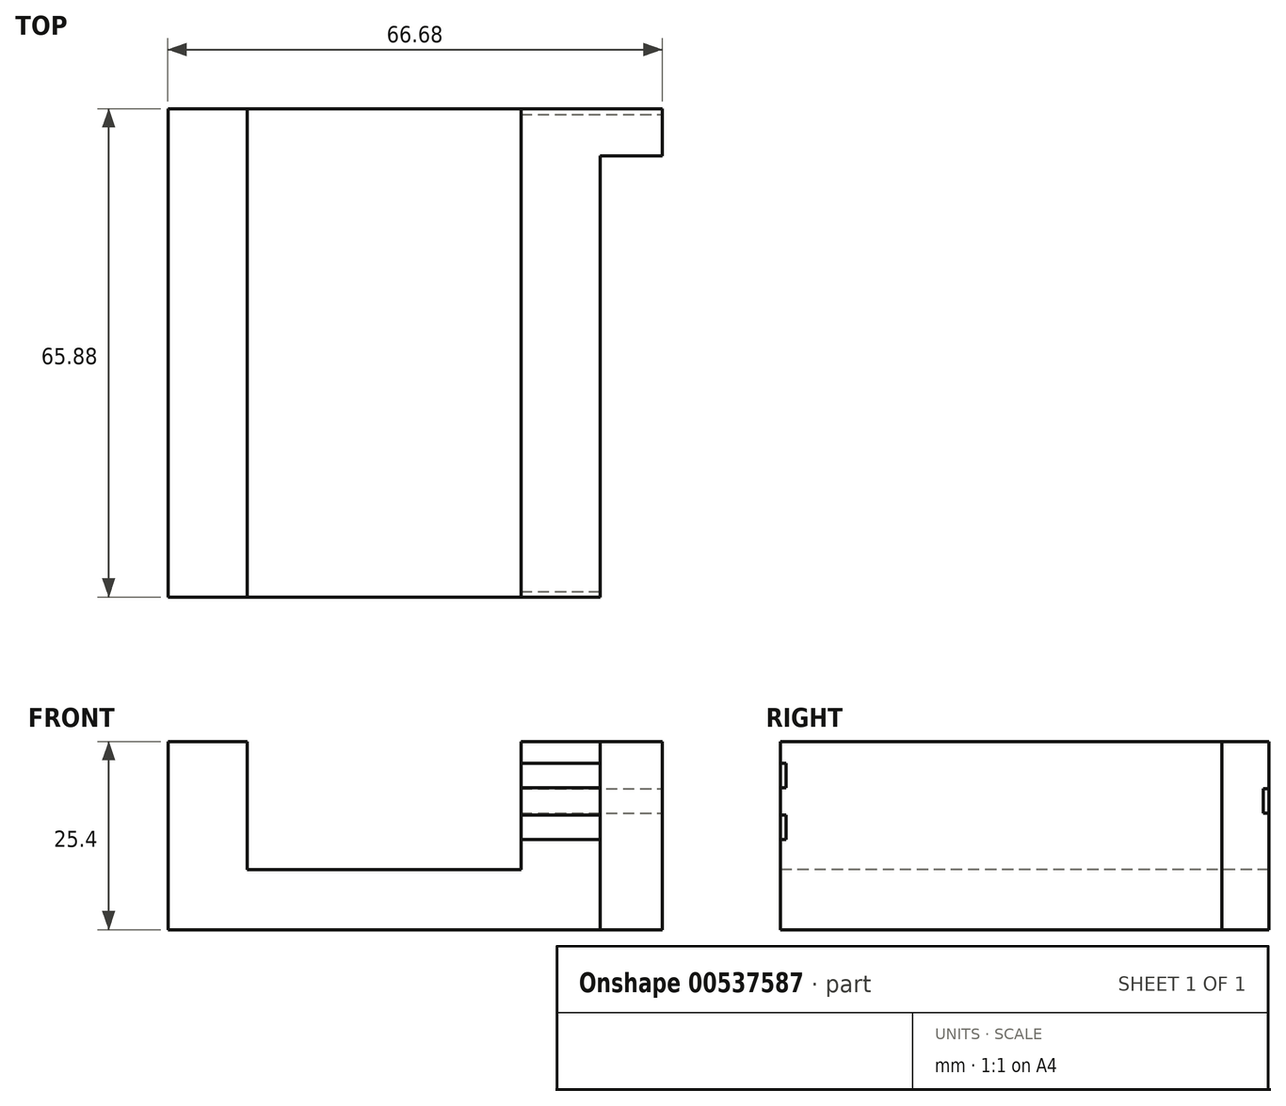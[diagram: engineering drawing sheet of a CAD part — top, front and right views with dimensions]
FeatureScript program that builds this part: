
annotation { "Feature Type Name" : "Feature", "Feature Type Description" : "" }
export const myFeature = defineFeature(function(context is Context, id is Id, definition is map)
    precondition{}
    {
        {
            var Q0;
            Q0=qCreatedBy(makeId("Top.planeOp"),FACE);
            var sketch = newSketch(context, id + "F0", { "sketchPlane" : qUnion([Q0])});
            skLineSegment(sketch, "E0.bottom", {"start": v(29.15, 32.94) * mm, "end": v(-1.9, 32.94) * mm});
            skLineSegment(sketch, "E0.top", {"start": v(29.15, -32.94) * mm, "end": v(9.65, -32.94) * mm});
            skLineSegment(sketch, "E0.right", {"start": v(-29.15, 32.94) * mm, "end": v(-29.15, -32.94) * mm});
            skPoint(sketch, "E0.middle", {"position": v(0, 0) * mm});
            skLineSegment(sketch, "E1", {"start": v(-18.48, 32.94) * mm, "end": v(-18.48, -32.94) * mm});
            skLineSegment(sketch, "E2", {"start": v(18.48, 32.94) * mm, "end": v(18.48, -32.94) * mm});
            skLineSegment(sketch, "E3.trimOffspring", {"start": v(-1.9, 32.94) * mm, "end": v(-29.15, 32.94) * mm});
            skLineSegment(sketch, "E4.trimOffspring", {"start": v(9.65, -32.94) * mm, "end": v(-9.65, -32.94) * mm});
            skLineSegment(sketch, "E5.trimOffspring", {"start": v(-9.65, -32.94) * mm, "end": v(-29.15, -32.94) * mm});
            skLineSegment(sketch, "E6", {"start": v(29.15, 32.94) * mm, "end": v(37.53, 32.94) * mm});
            skLineSegment(sketch, "E7", {"start": v(37.53, 32.94) * mm, "end": v(37.53, 26.6) * mm});
            skLineSegment(sketch, "E8", {"start": v(37.53, 26.6) * mm, "end": v(29.15, 26.6) * mm});
            skLineSegment(sketch, "E9", {"start": v(29.15, -20.24) * mm, "end": v(29.15, -32.94) * mm});
            skLineSegment(sketch, "E10", {"start": v(29.15, -20.24) * mm, "end": v(29.15, 32.94) * mm});
            skSolve(sketch);
        }
        {
            var Q0;
            {var subQ1=sQuery(id+"F0.wireOp",EDGE,"E1");Q0=makeQuery(id+"F0.imprint","IMPRINT",FACE,{"disambiguationData":[TD([[makeQuery(id+"F0.imprint","IMPRINT",EDGE,{"derivedFrom":subQ1}),1.0]])]});}
            extrude(context, id + "F1", {"entities" : qUnion([Q0]), "depth" : 8.13 * mm, "offsetDistance" : 25.4 * mm});
        }
        {
            var Q0;
            {var subQ0=sQuery(id+"F0.wireOp",EDGE,"E0.right");Q0=makeQuery(id+"F0.imprint","IMPRINT",FACE,{"disambiguationData":[TD([[makeQuery(id+"F0.imprint","IMPRINT",EDGE,{"derivedFrom":subQ0}),1.0]])]});}
            var Q1;
            {var subQ0=sQuery(id+"F0.wireOp",EDGE,"E0.left");Q1=makeQuery(id+"F0.imprint","IMPRINT",FACE,{"disambiguationData":[TD([[makeQuery(id+"F0.imprint","IMPRINT",EDGE,{"derivedFrom":subQ0}),-1.0]])]});}
            var Q2;
            {var subQ0=sQuery(id+"F0.wireOp",EDGE,"E6");Q2=makeQuery(id+"F0.imprint","IMPRINT",FACE,{"disambiguationData":[TD([[makeQuery(id+"F0.imprint","IMPRINT",EDGE,{"derivedFrom":subQ0}),-1.0]])]});}
            var Q3;
            {var subQ0=sQuery(id+"F0.wireOp",EDGE,"E2");Q3=makeQuery(id+"F0.imprint","IMPRINT",FACE,{"disambiguationData":[TD([[makeQuery(id+"F0.imprint","IMPRINT",EDGE,{"derivedFrom":subQ0}),1.0]])]});}
            extrude(context, id + "F2", {"entities" : qUnion([Q0, Q1, Q2, Q3]), "operationType" : NewBodyOperationType.ADD, "depth" : 25.4 * mm, "offsetDistance" : 25.4 * mm});
        }
        {
            var Q0;
            {var subQ0=sQuery(id+"F0.wireOp",EDGE,"E5.trimOffspring");var subQ1=sQuery(id+"F0.wireOp",EDGE,"E0.top");Q0=makeQuery(id+"F2.boolean.opBoolean","MERGE",FACE,{"derivedFrom":[makeQuery(id+"F1.opExtrude","SWEPT_FACE",FACE,{"disambiguationData":[OSD([subQ1,sQuery(id+"F0.wireOp",EDGE,"E4.trimOffspring"),subQ0])]}),makeQuery(id+"F2.opExtrude","SWEPT_FACE",FACE,{"disambiguationData":[OSD([subQ1])]}),makeQuery(id+"F2.opExtrude","SWEPT_FACE",FACE,{"disambiguationData":[OSD([subQ0])]})]});}
            var sketch = newSketch(context, id + "F3", { "sketchPlane" : qUnion([Q0])});
            skLineSegment(sketch, "E11", {"start": v(18.48, 22.48) * mm, "end": v(29.15, 22.48) * mm});
            skLineSegment(sketch, "E12", {"start": v(29.15, 19.18) * mm, "end": v(18.48, 19.18) * mm});
            skLineSegment(sketch, "E13", {"start": v(29.15, 15.5) * mm, "end": v(18.48, 15.5) * mm});
            skLineSegment(sketch, "E14", {"start": v(29.15, 12.2) * mm, "end": v(18.48, 12.2) * mm});
            skSolve(sketch);
        }
        {
            var Q0;
            {var subQ0=sQuery(id+"F3.wireOp",EDGE,"E13");Q0=makeQuery(id+"F3.imprint","IMPRINT",FACE,{"disambiguationData":[TD([[makeQuery(id+"F3.imprint","IMPRINT",EDGE,{"derivedFrom":subQ0}),1.0]])]});}
            var Q1;
            {var subQ0=sQuery(id+"F3.wireOp",EDGE,"E11");Q1=makeQuery(id+"F3.imprint","IMPRINT",FACE,{"disambiguationData":[TD([[makeQuery(id+"F3.imprint","IMPRINT",EDGE,{"derivedFrom":subQ0}),-1.0]])]});}
            extrude(context, id + "F4", {"entities" : qUnion([Q0, Q1]), "operationType" : NewBodyOperationType.REMOVE, "oppositeDirection" : true, "depth" : 0.76 * mm, "offsetDistance" : 25.4 * mm});
        }
        {
            var Q0;
            {var subQ0=sQuery(id+"F0.wireOp",EDGE,"E3.trimOffspring");var subQ1=sQuery(id+"F0.wireOp",EDGE,"E0.bottom");Q0=makeQuery(id+"F2.boolean.opBoolean","MERGE",FACE,{"derivedFrom":[makeQuery(id+"F1.opExtrude","SWEPT_FACE",FACE,{"disambiguationData":[OSD([subQ1,subQ0])]}),makeQuery(id+"F2.opExtrude","SWEPT_FACE",FACE,{"disambiguationData":[OSD([subQ1,sQuery(id+"F0.wireOp",EDGE,"E6")])]}),makeQuery(id+"F2.opExtrude","SWEPT_FACE",FACE,{"disambiguationData":[OSD([subQ0])]})]});}
            var sketch = newSketch(context, id + "F5", { "sketchPlane" : qUnion([Q0])});
            skLineSegment(sketch, "E15", {"start": v(-18.48, 19) * mm, "end": v(-37.53, 19) * mm});
            skLineSegment(sketch, "E16", {"start": v(-18.48, 15.7) * mm, "end": v(-37.53, 15.7) * mm});
            skSolve(sketch);
        }
        {
            var Q0;
            {var subQ0=sQuery(id+"F5.wireOp",EDGE,"E15");Q0=makeQuery(id+"F5.imprint","IMPRINT",FACE,{"disambiguationData":[TD([[makeQuery(id+"F5.imprint","IMPRINT",EDGE,{"derivedFrom":subQ0}),1.0]])]});}
            extrude(context, id + "F6", {"entities" : qUnion([Q0]), "operationType" : NewBodyOperationType.REMOVE, "oppositeDirection" : true, "depth" : 0.76 * mm, "offsetDistance" : 25.4 * mm});
        }
    });
